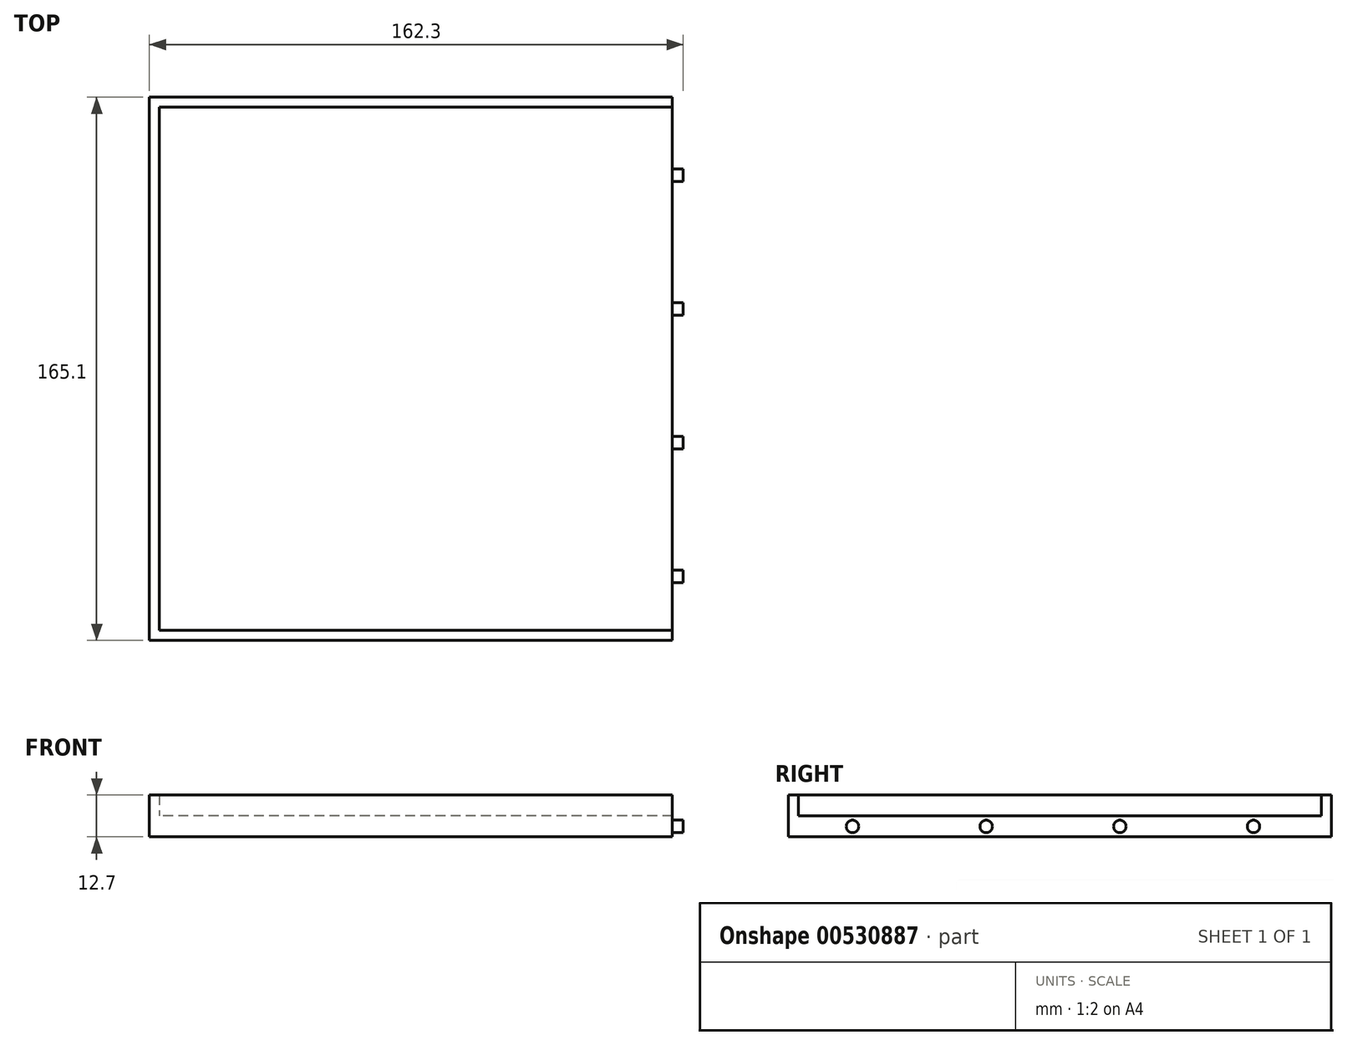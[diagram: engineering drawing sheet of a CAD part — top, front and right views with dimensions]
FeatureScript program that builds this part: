
annotation { "Feature Type Name" : "Feature", "Feature Type Description" : "" }
export const myFeature = defineFeature(function(context is Context, id is Id, definition is map)
    precondition{}
    {
        {
            var Q0;
            Q0=qCreatedBy(makeId("Top.planeOp"),FACE);
            var sketch = newSketch(context, id + "F0", { "sketchPlane" : qUnion([Q0])});
            skLineSegment(sketch, "E0.bottom", {"start": v(76.45, -79.5) * mm, "end": v(-76.45, -79.5) * mm});
            skLineSegment(sketch, "E0.top", {"start": v(76.45, 79.5) * mm, "end": v(-76.45, 79.5) * mm});
            skLineSegment(sketch, "E0.left", {"start": v(76.45, -79.5) * mm, "end": v(76.45, 79.5) * mm});
            skLineSegment(sketch, "E0.right", {"start": v(-76.45, -79.5) * mm, "end": v(-76.45, 79.5) * mm});
            skPoint(sketch, "E0.middle", {"position": v(0, 0) * mm});
            skLineSegment(sketch, "E1.0", {"start": v(79.5, 82.55) * mm, "end": v(-79.5, 82.55) * mm});
            skLineSegment(sketch, "E1.1", {"start": v(79.5, -82.55) * mm, "end": v(79.5, 82.55) * mm});
            skLineSegment(sketch, "E1.2", {"start": v(79.5, -82.55) * mm, "end": v(-79.5, -82.55) * mm});
            skLineSegment(sketch, "E1.3", {"start": v(-79.5, -82.55) * mm, "end": v(-79.5, 82.55) * mm});
            skLineSegment(sketch, "E2", {"start": v(76.45, 79.5) * mm, "end": v(79.5, 79.5) * mm});
            skLineSegment(sketch, "E3", {"start": v(76.45, -79.5) * mm, "end": v(79.5, -79.5) * mm});
            skSolve(sketch);
        }
        {
            var Q0;
            Q0=makeQuery(id+"F0.imprint","IMPRINT",FACE,{"disambiguationData":[TD([[makeQuery(id+"F0.imprint","IMPRINT",EDGE,{"derivedFrom":sQuery(id+"F0.wireOp",EDGE,"E0.bottom")}),-1.0]])]});
            extrude(context, id + "F1", {"entities" : qUnion([Q0]), "depth" : 6.35 * mm, "offsetDistance" : 25.4 * mm});
        }
        {
            var Q0;
            Q0=makeQuery(id+"F0.imprint","IMPRINT",FACE,{"disambiguationData":[TD([[makeQuery(id+"F0.imprint","IMPRINT",EDGE,{"derivedFrom":sQuery(id+"F0.wireOp",EDGE,"E0.bottom")}),1.0]])]});
            extrude(context, id + "F2", {"entities" : qUnion([Q0]), "operationType" : NewBodyOperationType.ADD, "depth" : 12.7 * mm, "offsetDistance" : 25.4 * mm});
        }
        {
            var Q0;
            Q0=makeQuery(id+"F1.opExtrude","SWEPT_FACE",FACE,{"disambiguationData":[OSD([sQuery(id+"F0.wireOp",EDGE,"E0.left")])]});
            var sketch = newSketch(context, id + "F3", { "sketchPlane" : qUnion([Q0])});
            skLineSegment(sketch, "E4", {"start": v(-79.5, 3.18) * mm, "end": v(79.5, 3.18) * mm, "construction": true});
            skCircle(sketch, "E5", {"center": v(-63.08, 3.18) * mm, "radius": 1.9 * mm});
            skCircle(sketch, "E6.1.0.0", {"center": v(-22.44, 3.18) * mm, "radius": 1.9 * mm});
            skCircle(sketch, "E6.2.0.0", {"center": v(18.2, 3.18) * mm, "radius": 1.9 * mm});
            skCircle(sketch, "E6.3.0.0", {"center": v(58.84, 3.18) * mm, "radius": 1.9 * mm});
            skLineSegment(sketch, "E6.direction1", {"start": v(-63.08, 3.18) * mm, "end": v(-22.44, 3.18) * mm, "construction": true});
            skSolve(sketch);
        }
        {
            var Q0;
            Q0 = qSketchRegion(id + "F3", true);
            extrude(context, id + "F4", {"entities" : qUnion([Q0]), "operationType" : NewBodyOperationType.ADD, "depth" : 6.35 * mm, "offsetDistance" : 25.4 * mm});
        }
        {
            var Q0;
            Q0=makeQuery(id+"F0.imprint","IMPRINT",FACE,{"disambiguationData":[TD([[makeQuery(id+"F0.imprint","IMPRINT",EDGE,{"derivedFrom":sQuery(id+"F0.wireOp",EDGE,"E0.left")}),-1.0]])]});
            extrude(context, id + "F5", {"entities" : qUnion([Q0]), "operationType" : NewBodyOperationType.ADD, "depth" : 6.35 * mm, "offsetDistance" : 25.4 * mm});
        }
    });
